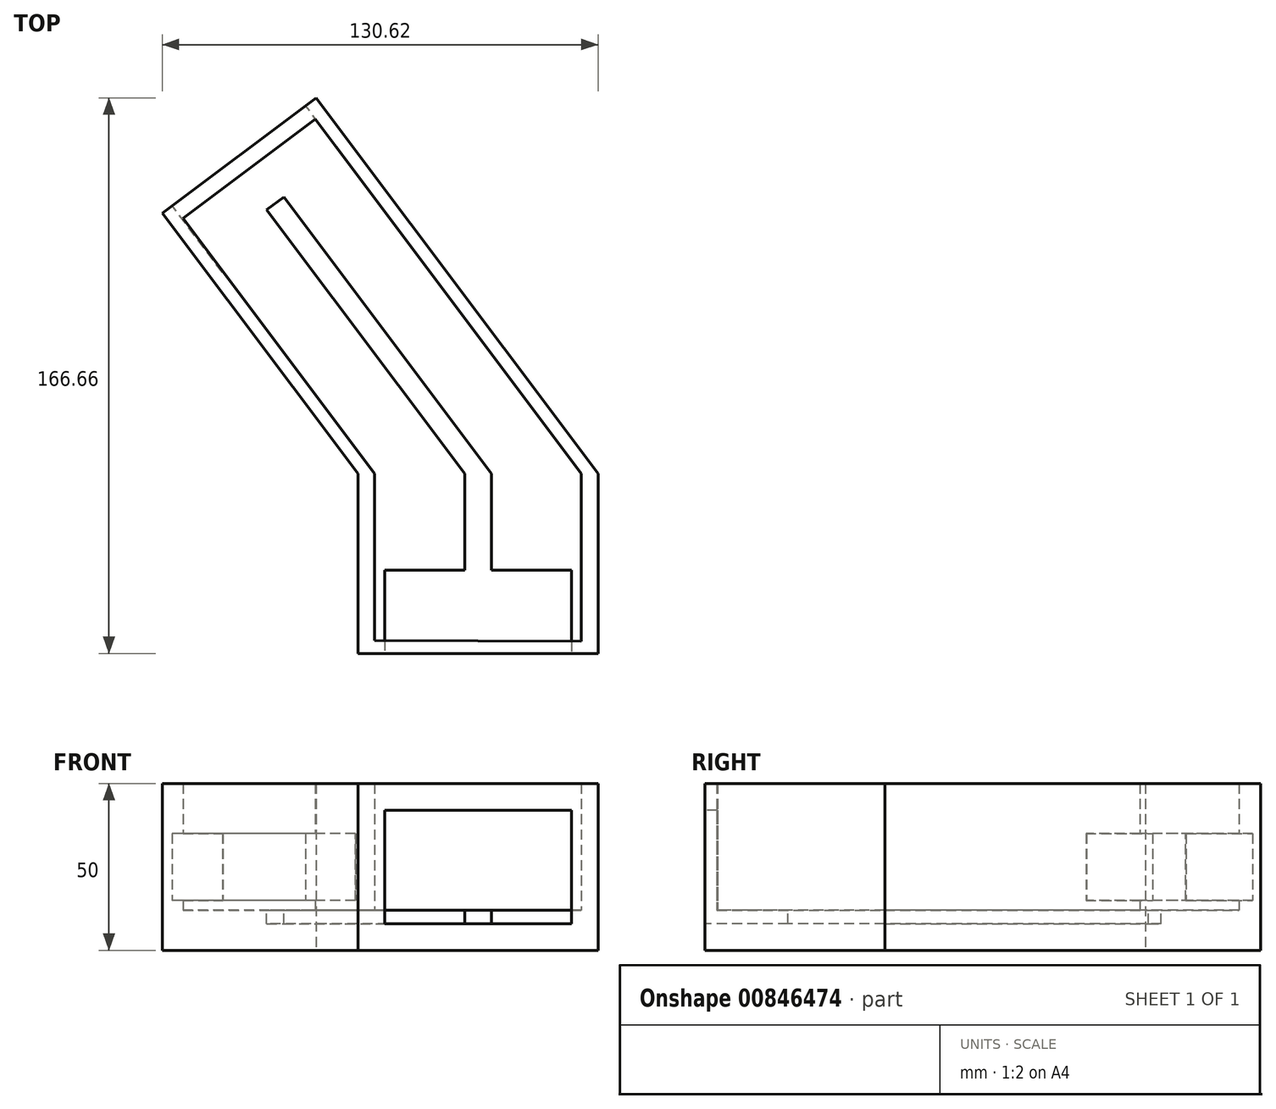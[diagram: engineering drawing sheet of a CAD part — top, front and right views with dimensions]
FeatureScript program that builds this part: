
annotation { "Feature Type Name" : "Feature", "Feature Type Description" : "" }
export const myFeature = defineFeature(function(context is Context, id is Id, definition is map)
    precondition{}
    {
        {
            var Q0;
            Q0=qCreatedBy(makeId("Top.planeOp"),FACE);
            var sketch = newSketch(context, id + "F0", { "sketchPlane" : qUnion([Q0])});
            skLineSegment(sketch, "E0", {"start": v(44.66, -54) * mm, "end": v(-27.34, -54) * mm});
            skLineSegment(sketch, "E1", {"start": v(-27.34, -54) * mm, "end": v(-27.34, -50) * mm});
            skLineSegment(sketch, "E2", {"start": v(-27.34, -50) * mm, "end": v(-27.34, -50) * mm});
            skLineSegment(sketch, "E3", {"start": v(-27.34, -50) * mm, "end": v(-27.34, 0) * mm});
            skLineSegment(sketch, "E4", {"start": v(-27.34, 0) * mm, "end": v(-85.96, 78.08) * mm});
            skLineSegment(sketch, "E5", {"start": v(-85.96, 78.08) * mm, "end": v(-39.92, 112.66) * mm});
            skLineSegment(sketch, "E6", {"start": v(-39.92, 112.66) * mm, "end": v(44.66, 0) * mm});
            skLineSegment(sketch, "E7", {"start": v(44.66, 0) * mm, "end": v(44.66, -50) * mm});
            skLineSegment(sketch, "E8", {"start": v(44.66, -50) * mm, "end": v(44.66, -50) * mm});
            skLineSegment(sketch, "E9", {"start": v(44.66, -50) * mm, "end": v(44.66, -54) * mm});
            skLineSegment(sketch, "E10", {"start": v(-22.34, -50.1) * mm, "end": v(-22.34, 0) * mm});
            skLineSegment(sketch, "E11", {"start": v(-22.34, 0) * mm, "end": v(-79.76, 76.49) * mm});
            skLineSegment(sketch, "E12", {"start": v(-79.76, 76.49) * mm, "end": v(-40.12, 106.26) * mm});
            skLineSegment(sketch, "E13", {"start": v(-40.12, 106.26) * mm, "end": v(39.66, 0) * mm});
            skLineSegment(sketch, "E14", {"start": v(39.66, 0) * mm, "end": v(39.66, -50.37) * mm});
            skLineSegment(sketch, "E15", {"start": v(39.66, -50.37) * mm, "end": v(-22.34, -50.1) * mm});
            skSolve(sketch);
        }
        {
            var Q0;
            Q0=makeQuery(id+"F0.imprint","IMPRINT",FACE,{"disambiguationData":[TD([[makeQuery(id+"F0.imprint","IMPRINT",EDGE,{"derivedFrom":sQuery(id+"F0.wireOp",EDGE,"E10")}),-1.0]])]});
            var Q1;
            Q1=makeQuery(id+"F0.imprint","IMPRINT",FACE,{"disambiguationData":[TD([[makeQuery(id+"F0.imprint","IMPRINT",EDGE,{"derivedFrom":sQuery(id+"F0.wireOp",EDGE,"E0")}),-1.0]])]});
            extrude(context, id + "F1", {"entities" : qUnion([Q0, Q1]), "depth" : 12 * mm, "offsetDistance" : 25 * mm});
        }
        {
            var Q0;
            Q0 = qSketchRegion(id + "F0", true);
            extrude(context, id + "F2", {"entities" : qUnion([Q0]), "operationType" : NewBodyOperationType.ADD, "depth" : 50 * mm, "offsetDistance" : 25 * mm});
        }
        {
            var Q0;
            {var subQ0=sQuery(id+"F0.wireOp",EDGE,"E0");Q0=makeQuery(id+"F2.boolean.opBoolean","MERGE",FACE,{"derivedFrom":[makeQuery(id+"F1.opExtrude","SWEPT_FACE",FACE,{"disambiguationData":[OSD([subQ0])]}),makeQuery(id+"F2.opExtrude","SWEPT_FACE",FACE,{"disambiguationData":[OSD([subQ0])]})]});}
            var sketch = newSketch(context, id + "F3", { "sketchPlane" : qUnion([Q0])});
            skLineSegment(sketch, "E16.bottom", {"start": v(-19.34, 42) * mm, "end": v(36.66, 42) * mm});
            skLineSegment(sketch, "E16.top", {"start": v(-19.34, 8) * mm, "end": v(36.66, 8) * mm});
            skLineSegment(sketch, "E16.left", {"start": v(-19.34, 42) * mm, "end": v(-19.34, 8) * mm});
            skLineSegment(sketch, "E16.right", {"start": v(36.66, 42) * mm, "end": v(36.66, 8) * mm});
            skSolve(sketch);
        }
        {
            var Q0;
            Q0=makeQuery(id+"F3.imprint","IMPRINT",FACE,{"disambiguationData":[TD([[makeQuery(id+"F3.imprint","IMPRINT",EDGE,{"derivedFrom":sQuery(id+"F3.wireOp",EDGE,"E16.bottom")}),-1.0]])]});
            extrude(context, id + "F4", {"entities" : qUnion([Q0]), "operationType" : NewBodyOperationType.REMOVE, "oppositeDirection" : true, "depth" : 25 * mm, "offsetDistance" : 25 * mm});
        }
        {
            var Q0;
            {var subQ0=sQuery(id+"F0.wireOp",EDGE,"E5");Q0=makeQuery(id+"F2.boolean.opBoolean","MERGE",FACE,{"derivedFrom":[makeQuery(id+"F1.opExtrude","SWEPT_FACE",FACE,{"disambiguationData":[OSD([subQ0])]}),makeQuery(id+"F2.opExtrude","SWEPT_FACE",FACE,{"disambiguationData":[OSD([subQ0])]})]});}
            var sketch = newSketch(context, id + "F5", { "sketchPlane" : qUnion([Q0])});
            skLineSegment(sketch, "E17.bottom", {"start": v(-31.85, 35) * mm, "end": v(18.15, 35) * mm});
            skLineSegment(sketch, "E17.top", {"start": v(-31.85, 15) * mm, "end": v(18.15, 15) * mm});
            skLineSegment(sketch, "E17.left", {"start": v(-31.85, 35) * mm, "end": v(-31.85, 15) * mm});
            skLineSegment(sketch, "E17.right", {"start": v(18.15, 35) * mm, "end": v(18.15, 15) * mm});
            skSolve(sketch);
        }
        {
            var Q0;
            Q0=makeQuery(id+"F5.imprint","IMPRINT",FACE,{"disambiguationData":[TD([[makeQuery(id+"F5.imprint","IMPRINT",EDGE,{"derivedFrom":sQuery(id+"F5.wireOp",EDGE,"E17.bottom")}),-1.0]])]});
            extrude(context, id + "F6", {"entities" : qUnion([Q0]), "operationType" : NewBodyOperationType.REMOVE, "oppositeDirection" : true, "depth" : 25 * mm, "offsetDistance" : 25 * mm});
        }
        {
            var Q0;
            Q0=makeQuery(id+"F1.opExtrude","CAP_FACE",FACE,{"disambiguationData":[OSD([sQuery(id+"F0.wireOp",EDGE,"E0"),sQuery(id+"F0.wireOp",EDGE,"E1"),sQuery(id+"F0.wireOp",EDGE,"E3"),sQuery(id+"F0.wireOp",EDGE,"E4"),sQuery(id+"F0.wireOp",EDGE,"E5"),sQuery(id+"F0.wireOp",EDGE,"E6"),sQuery(id+"F0.wireOp",EDGE,"E7"),sQuery(id+"F0.wireOp",EDGE,"E9")])],"isStart":false});
            var sketch = newSketch(context, id + "F7", { "sketchPlane" : qUnion([Q0])});
            skLineSegment(sketch, "E18", {"start": v(-54.7, 79.06) * mm, "end": v(-49.58, 82.9) * mm});
            skLineSegment(sketch, "E19", {"start": v(-49.58, 82.9) * mm, "end": v(12.66, 0) * mm});
            skLineSegment(sketch, "E20", {"start": v(12.66, 0) * mm, "end": v(12.66, -29) * mm});
            skLineSegment(sketch, "E21", {"start": v(12.66, -29) * mm, "end": v(4.66, -29) * mm});
            skLineSegment(sketch, "E22", {"start": v(4.66, -29) * mm, "end": v(4.66, 0) * mm});
            skLineSegment(sketch, "E23", {"start": v(4.66, 0) * mm, "end": v(-54.7, 79.06) * mm});
            skSolve(sketch);
        }
        {
            var Q0;
            Q0=makeQuery(id+"F7.imprint","IMPRINT",FACE,{"disambiguationData":[TD([[makeQuery(id+"F7.imprint","IMPRINT",EDGE,{"derivedFrom":sQuery(id+"F7.wireOp",EDGE,"E18")}),-1.0]])]});
            extrude(context, id + "F8", {"entities" : qUnion([Q0]), "operationType" : NewBodyOperationType.REMOVE, "oppositeDirection" : true, "depth" : 4 * mm, "offsetDistance" : 25 * mm});
        }
    });
